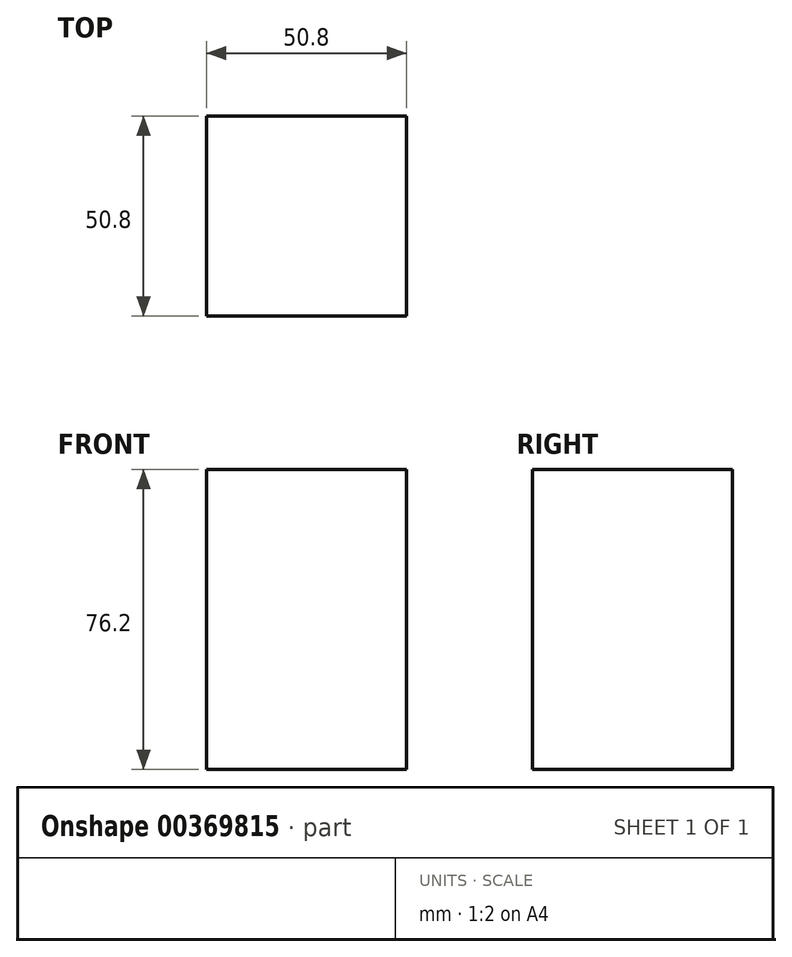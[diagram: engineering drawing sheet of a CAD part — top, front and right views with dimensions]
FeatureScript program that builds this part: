
annotation { "Feature Type Name" : "Feature", "Feature Type Description" : "" }
export const myFeature = defineFeature(function(context is Context, id is Id, definition is map)
    precondition{}
    {
        {
            var Q0;
            Q0=qCreatedBy(makeId("Front.planeOp"),FACE);
            var sketch = newSketch(context, id + "F0", { "sketchPlane" : qUnion([Q0])});
            skLineSegment(sketch, "E0.bottom", {"start": v(-31.99, 40.12) * mm, "end": v(18.81, 40.12) * mm});
            skLineSegment(sketch, "E0.top", {"start": v(-31.99, -36.08) * mm, "end": v(18.81, -36.08) * mm});
            skLineSegment(sketch, "E0.left", {"start": v(-31.99, 40.12) * mm, "end": v(-31.99, -36.08) * mm});
            skLineSegment(sketch, "E0.right", {"start": v(18.81, 40.12) * mm, "end": v(18.81, -36.08) * mm});
            skSolve(sketch);
        }
        {
            var Q0;
            Q0 = qSketchRegion(id + "F0", true);
            extrude(context, id + "F1", {"entities" : qUnion([Q0]), "depth" : 50.8 * mm});
        }
        {
            var Q0;
            Q0=makeQuery(id+"F1.opExtrude","CAP_FACE",FACE,{"disambiguationData":[OSD([sQuery(id+"F0.wireOp",EDGE,"E0.bottom"),sQuery(id+"F0.wireOp",EDGE,"E0.top"),sQuery(id+"F0.wireOp",EDGE,"E0.left"),sQuery(id+"F0.wireOp",EDGE,"E0.right")])],"isStart":true});
            var sketch = newSketch(context, id + "F2", { "sketchPlane" : qUnion([Q0])});
            skCircle(sketch, "E1", {"center": v(7.23, 13.11) * mm, "radius": 10.18 * mm});
            skSolve(sketch);
        }
        {
            var Q0;
            Q0=sQuery(id+"F2.wireOp",EDGE,"E1");
            extrude(context, id + "F3", {"bodyType" : ToolBodyType.SURFACE, "surfaceEntities" : qUnion([Q0]), "depth" : 25.4 * mm});
        }
    });
